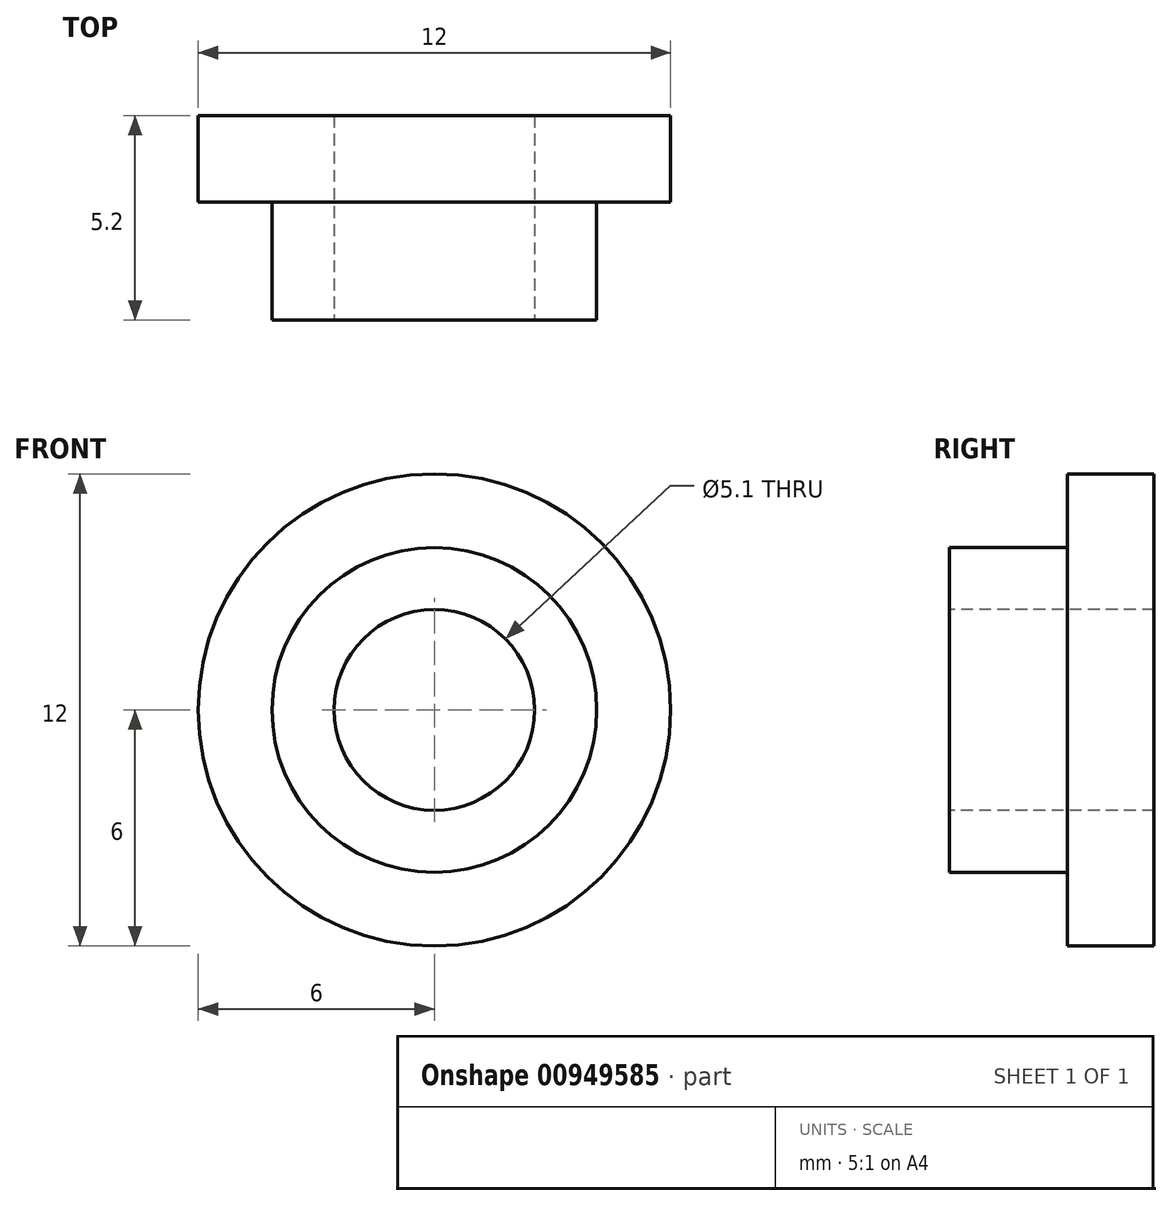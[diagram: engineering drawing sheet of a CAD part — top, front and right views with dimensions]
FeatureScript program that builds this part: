
annotation { "Feature Type Name" : "Feature", "Feature Type Description" : "" }
export const myFeature = defineFeature(function(context is Context, id is Id, definition is map)
    precondition{}
    {
        {
            var Q0;
            Q0=qCreatedBy(makeId("Front.planeOp"),FACE);
            var sketch = newSketch(context, id + "F0", { "sketchPlane" : qUnion([Q0])});
            skCircle(sketch, "E0", {"center": v(0, 0) * mm, "radius": 6 * mm});
            skSolve(sketch);
        }
        {
            var Q0;
            Q0 = qSketchRegion(id + "F0", true);
            extrude(context, id + "F1", {"entities" : qUnion([Q0]), "depth" : 2.2 * mm, "offsetDistance" : 25 * mm});
        }
        {
            var Q0;
            Q0=makeQuery(id+"F1.opExtrude","CAP_FACE",FACE,{"disambiguationData":[OSD([sQuery(id+"F0.wireOp",EDGE,"E0")])],"isStart":false});
            var sketch = newSketch(context, id + "F2", { "sketchPlane" : qUnion([Q0])});
            skCircle(sketch, "E1", {"center": v(0, 0) * mm, "radius": 4.12 * mm});
            skSolve(sketch);
        }
        {
            var Q0;
            Q0 = qSketchRegion(id + "F2", true);
            extrude(context, id + "F3", {"entities" : qUnion([Q0]), "operationType" : NewBodyOperationType.ADD, "depth" : 3 * mm, "offsetDistance" : 25 * mm});
        }
        {
            var Q0;
            Q0=makeQuery(id+"F3.opExtrude","CAP_FACE",FACE,{"disambiguationData":[OSD([sQuery(id+"F2.wireOp",EDGE,"E1")])],"isStart":false});
            var sketch = newSketch(context, id + "F4", { "sketchPlane" : qUnion([Q0])});
            skCircle(sketch, "E2", {"center": v(0, 0) * mm, "radius": 2.55 * mm});
            skSolve(sketch);
        }
        {
            var Q0;
            Q0=makeQuery(id+"F4.imprint","IMPRINT",FACE,{"disambiguationData":[TD([[makeQuery(id+"F4.imprint","IMPRINT",EDGE,{"derivedFrom":sQuery(id+"F4.wireOp",EDGE,"E2")}),1.0]])]});
            var Q1;
            Q1=sQuery(id+"F4.wireOp",EDGE,"E2");
            var Q2;
            Q2=makeQuery(id+"F1.opExtrude","CAP_FACE",FACE,{"disambiguationData":[OSD([sQuery(id+"F0.wireOp",EDGE,"E0")])],"isStart":true});
            extrude(context, id + "F5", {"entities" : qUnion([Q0]), "operationType" : NewBodyOperationType.REMOVE, "surfaceEntities" : qUnion([Q1]), "endBound" : BoundingType.UP_TO_SURFACE, "oppositeDirection" : true, "depth" : 25 * mm, "endBoundEntityFace" : qUnion([Q2]), "offsetDistance" : 25 * mm});
        }
    });
